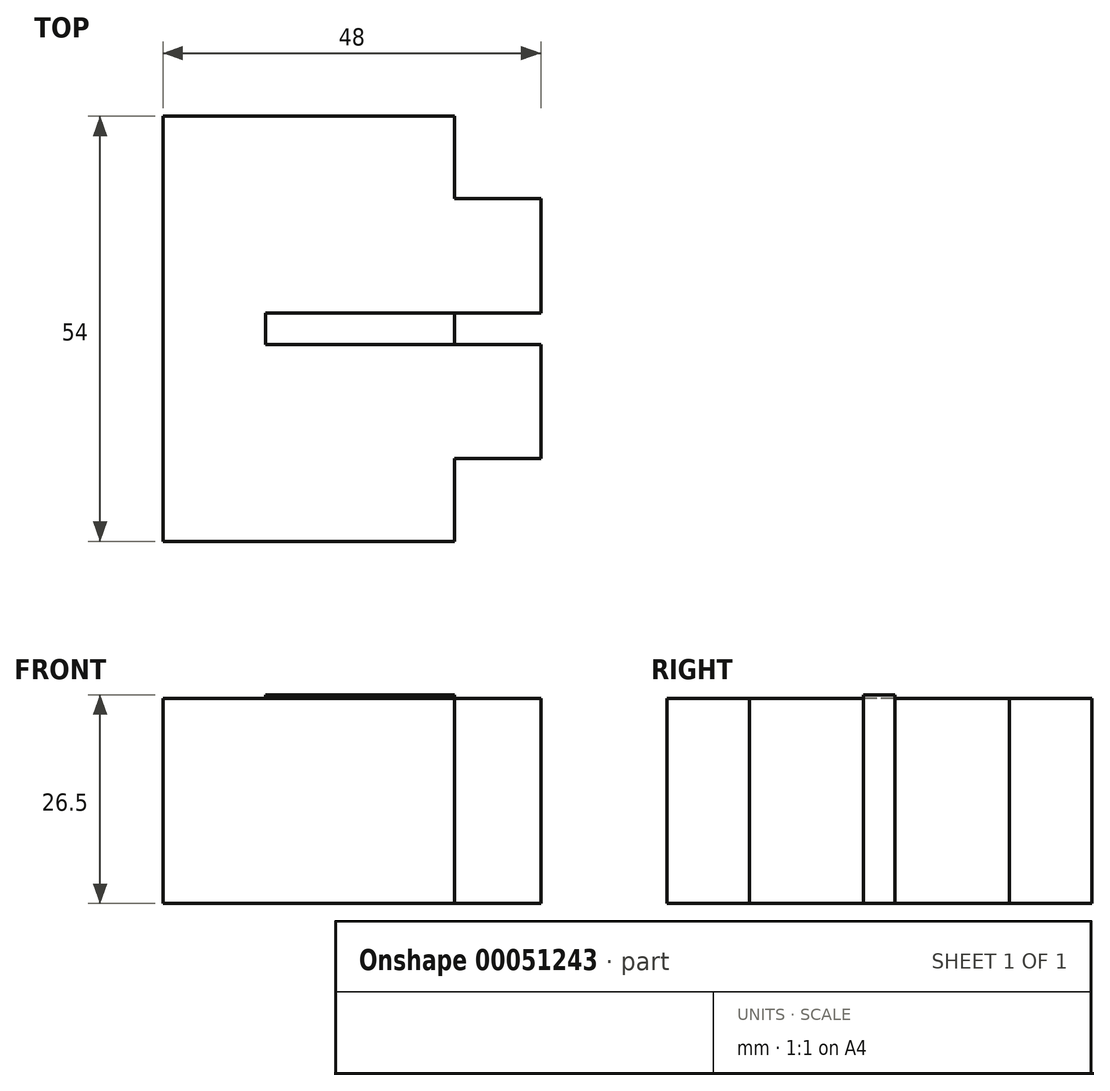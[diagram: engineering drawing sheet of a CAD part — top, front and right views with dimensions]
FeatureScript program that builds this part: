
annotation { "Feature Type Name" : "Feature", "Feature Type Description" : "" }
export const myFeature = defineFeature(function(context is Context, id is Id, definition is map)
    precondition{}
    {
        {
            var Q0;
            Q0=qCreatedBy(makeId("Top.planeOp"),FACE);
            var sketch = newSketch(context, id + "F0", { "sketchPlane" : qUnion([Q0])});
            skLineSegment(sketch, "E0.bottom", {"start": v(0, 0) * mm, "end": v(37, 0) * mm});
            skLineSegment(sketch, "E0.top", {"start": v(0, -54) * mm, "end": v(37, -54) * mm});
            skLineSegment(sketch, "E0.left", {"start": v(0, 0) * mm, "end": v(0, -54) * mm});
            skLineSegment(sketch, "E0.right", {"start": v(37, 0) * mm, "end": v(37, -10.5) * mm});
            skLineSegment(sketch, "E1.bottom", {"start": v(37, -10.5) * mm, "end": v(48, -10.5) * mm});
            skLineSegment(sketch, "E1.top", {"start": v(37, -43.5) * mm, "end": v(48, -43.5) * mm});
            skLineSegment(sketch, "E1.left", {"start": v(37, -10.5) * mm, "end": v(37, -27) * mm});
            skLineSegment(sketch, "E1.right", {"start": v(48, -10.5) * mm, "end": v(48, -43.5) * mm});
            skLineSegment(sketch, "E2.trimOffspring", {"start": v(37, -27) * mm, "end": v(37, -54) * mm});
            skLineSegment(sketch, "E3.bottom", {"start": v(13, -25) * mm, "end": v(48, -25) * mm});
            skLineSegment(sketch, "E3.top", {"start": v(13, -29) * mm, "end": v(48, -29) * mm});
            skLineSegment(sketch, "E3.left", {"start": v(13, -25) * mm, "end": v(13, -29) * mm});
            skLineSegment(sketch, "E3.right", {"start": v(48, -25) * mm, "end": v(48, -29) * mm});
            skPoint(sketch, "E4", {"position": v(48, -27) * mm});
            skSolve(sketch);
        }
        {
            var Q0;
            Q0=makeQuery(id+"F0.imprint","IMPRINT",FACE,{"disambiguationData":[TD([[makeQuery(id+"F0.imprint","IMPRINT",EDGE,{"derivedFrom":sQuery(id+"F0.wireOp",EDGE,"E0.bottom")}),-1.0]])]});
            var Q1;
            {var subQ0=sQuery(id+"F0.wireOp",EDGE,"E1.bottom");Q1=makeQuery(id+"F0.imprint","IMPRINT",FACE,{"disambiguationData":[TD([[makeQuery(id+"F0.imprint","IMPRINT",EDGE,{"derivedFrom":subQ0}),-1.0]])]});}
            var Q2;
            {var subQ0=sQuery(id+"F0.wireOp",EDGE,"E1.top");Q2=makeQuery(id+"F0.imprint","IMPRINT",FACE,{"disambiguationData":[TD([[makeQuery(id+"F0.imprint","IMPRINT",EDGE,{"derivedFrom":subQ0}),1.0]])]});}
            extrude(context, id + "F1", {"entities" : qUnion([Q0, Q1, Q2]), "depth" : 26 * mm});
        }
        {
            var Q0;
            {var subQ0=sQuery(id+"F0.wireOp",EDGE,"E3.left");Q0=makeQuery(id+"F0.imprint","IMPRINT",FACE,{"disambiguationData":[TD([[makeQuery(id+"F0.imprint","IMPRINT",EDGE,{"derivedFrom":subQ0}),1.0]])]});}
            var Q1;
            {var subQ0=sQuery(id+"F0.wireOp",EDGE,"E3.right");Q1=makeQuery(id+"F0.imprint","IMPRINT",FACE,{"disambiguationData":[TD([[makeQuery(id+"F0.imprint","IMPRINT",EDGE,{"derivedFrom":subQ0}),-1.0]])]});}
            extrude(context, id + "F2", {"entities" : qUnion([Q0, Q1]), "operationType" : NewBodyOperationType.ADD, "depth" : 26.5 * mm});
        }
    });
